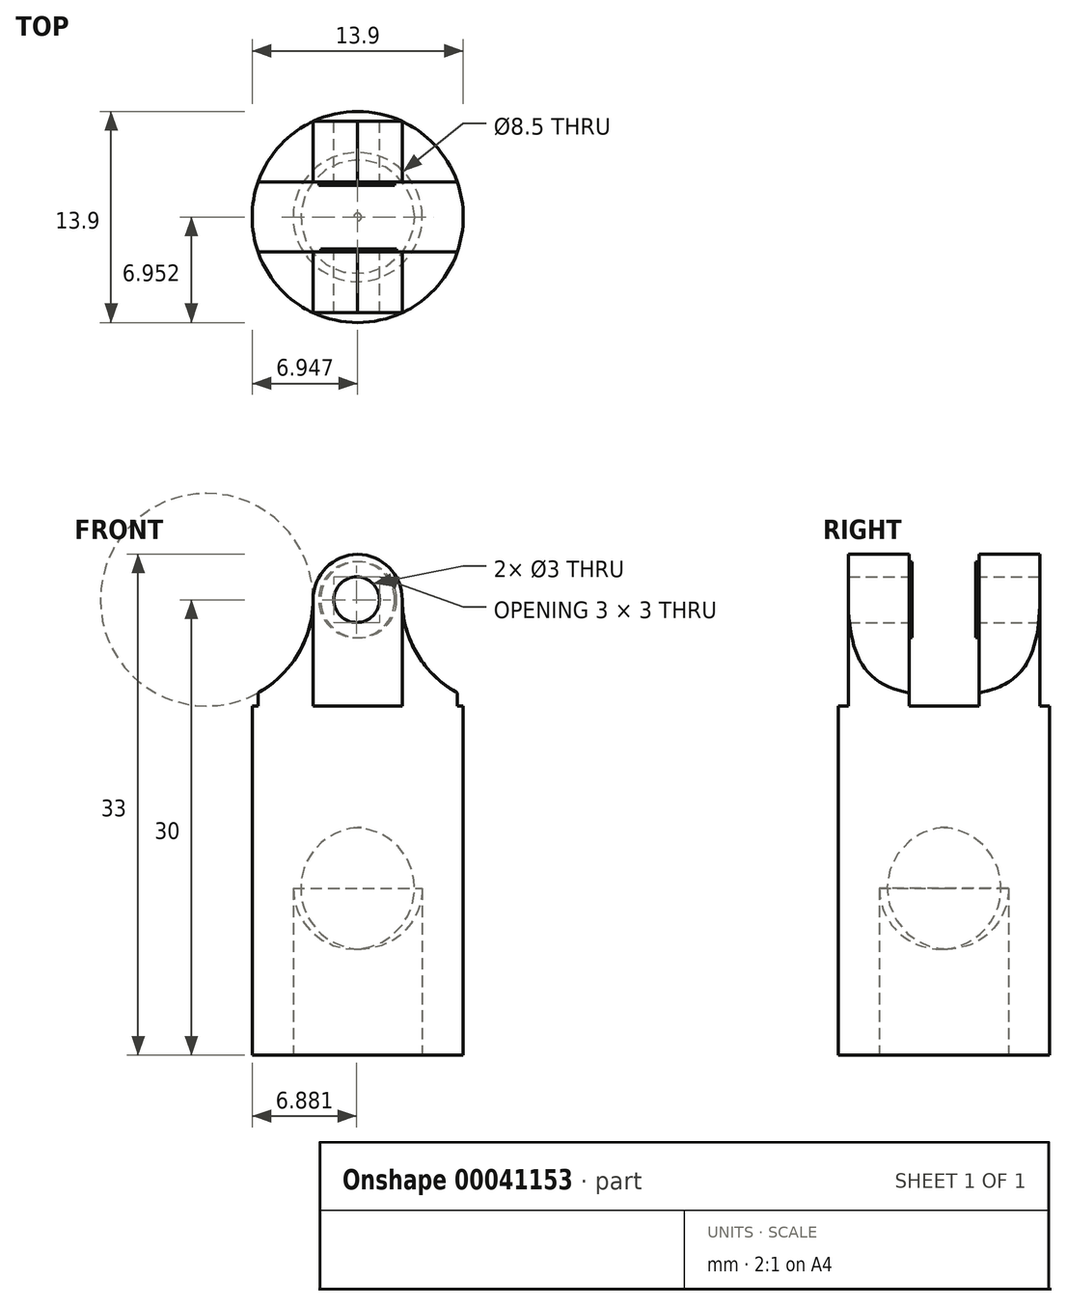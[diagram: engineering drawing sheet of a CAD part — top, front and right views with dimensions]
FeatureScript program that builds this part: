
annotation { "Feature Type Name" : "Feature", "Feature Type Description" : "" }
export const myFeature = defineFeature(function(context is Context, id is Id, definition is map)
    precondition{}
    {
        {
            var Q0;
            Q0=qCreatedBy(makeId("Top.planeOp"),FACE);
            var sketch = newSketch(context, id + "F0", { "sketchPlane" : qUnion([Q0])});
            skLineSegment(sketch, "E0", {"start": v(0, -0.07) * mm, "end": v(-0.27, -0.07) * mm});
            skPoint(sketch, "E1.visualSharp", {"position": v(-9.62, 20.9) * mm});
            skCircle(sketch, "E2", {"center": v(-16.02, 6.95) * mm, "radius": 6.95 * mm});
            skSolve(sketch);
        }
        {
            var Q0;
            Q0 = qSketchRegion(id + "F0", true);
            extrude(context, id + "F1", {"entities" : qUnion([Q0]), "depth" : 23 * mm});
        }
        {
            var Q0;
            Q0=makeQuery(id+"F1.opExtrude","CAP_FACE",FACE,{"disambiguationData":[OSD([sQuery(id+"F0.wireOp",EDGE,"E2")])],"isStart":false});
            var sketch = newSketch(context, id + "F2", { "sketchPlane" : qUnion([Q0])});
            skLineSegment(sketch, "E3", {"start": v(-16.02, 6.95) * mm, "end": v(-9.07, 6.95) * mm});
            skLineSegment(sketch, "E4", {"start": v(-16.02, 6.95) * mm, "end": v(-22.97, 6.95) * mm});
            skLineSegment(sketch, "E5", {"start": v(-22.58, 4.65) * mm, "end": v(-9.47, 4.65) * mm});
            skLineSegment(sketch, "E6", {"start": v(-9.47, 9.25) * mm, "end": v(-22.58, 9.25) * mm});
            skLineSegment(sketch, "E7", {"start": v(-16.02, 6.95) * mm, "end": v(-16.02, 0) * mm});
            skLineSegment(sketch, "E8", {"start": v(-13.09, 0.65) * mm, "end": v(-18.96, 0.65) * mm});
            skLineSegment(sketch, "E9", {"start": v(-13.09, 13.25) * mm, "end": v(-18.96, 13.25) * mm});
            skLineSegment(sketch, "E10", {"start": v(-16.02, 6.95) * mm, "end": v(-16.02, 13.25) * mm});
            skLineSegment(sketch, "E11", {"start": v(-13.09, 13.25) * mm, "end": v(-13.09, 9.25) * mm});
            skLineSegment(sketch, "E12", {"start": v(-13.09, 0.65) * mm, "end": v(-13.09, 4.65) * mm});
            skLineSegment(sketch, "E13", {"start": v(-18.96, 0.65) * mm, "end": v(-18.96, 4.65) * mm});
            skLineSegment(sketch, "E14", {"start": v(-18.96, 13.25) * mm, "end": v(-18.96, 9.25) * mm});
            skSolve(sketch);
        }
        {
            var Q0;
            Q0 = qSketchRegion(id + "F2", true);
            extrude(context, id + "F3", {"entities" : qUnion([Q0]), "operationType" : NewBodyOperationType.ADD, "depth" : 10 * mm});
        }
        {
            var Q0;
            Q0=makeQuery(id+"F3.opExtrude","CAP_EDGE",EDGE,{"disambiguationData":[OSD([sQuery(id+"F2.wireOp",EDGE,"E12")])],"isStart":false});
            var Q1;
            Q1=makeQuery(id+"F3.opExtrude","CAP_EDGE",EDGE,{"disambiguationData":[OSD([sQuery(id+"F2.wireOp",EDGE,"E11")])],"isStart":false});
            var Q2;
            Q2=makeQuery(id+"F3.opExtrude","CAP_EDGE",EDGE,{"disambiguationData":[OSD([sQuery(id+"F2.wireOp",EDGE,"E14")])],"isStart":false});
            var Q3;
            Q3=makeQuery(id+"F3.opExtrude","CAP_EDGE",EDGE,{"disambiguationData":[OSD([sQuery(id+"F2.wireOp",EDGE,"E13")])],"isStart":false});
            fillet(context, id + "F4", {"entities" : qUnion([Q0, Q1, Q2, Q3]), "radius" : 3 * mm, "tangentPropagation" : true, "allowEdgeOverflow" : false});
        }
        {
            var Q0;
            Q0=makeQuery(id+"F3.opExtrude","CAP_EDGE",EDGE,{"disambiguationData":[OSD([sQuery(id+"F2.wireOp",EDGE,"E12")])],"isStart":true});
            var Q1;
            Q1=makeQuery(id+"F3.opExtrude","CAP_EDGE",EDGE,{"disambiguationData":[OSD([sQuery(id+"F2.wireOp",EDGE,"E11")])],"isStart":true});
            var Q2;
            Q2=makeQuery(id+"F3.opExtrude","CAP_EDGE",EDGE,{"disambiguationData":[OSD([sQuery(id+"F2.wireOp",EDGE,"E14")])],"isStart":true});
            var Q3;
            Q3=makeQuery(id+"F3.opExtrude","CAP_EDGE",EDGE,{"disambiguationData":[OSD([sQuery(id+"F2.wireOp",EDGE,"E13")])],"isStart":true});
            fillet(context, id + "F5", {"entities" : qUnion([Q0, Q1, Q2, Q3]), "radius" : 7 * mm, "tangentPropagation" : true, "allowEdgeOverflow" : false});
        }
        {
            var Q0;
            Q0=makeQuery(id+"F1.opExtrude","CAP_FACE",FACE,{"disambiguationData":[OSD([sQuery(id+"F0.wireOp",EDGE,"E2")])],"isStart":true});
            var sketch = newSketch(context, id + "F6", { "sketchPlane" : qUnion([Q0])});
            skCircle(sketch, "E15", {"center": v(-16.02, -6.95) * mm, "radius": 4.25 * mm});
            skSolve(sketch);
        }
        {
            var Q0;
            Q0 = qSketchRegion(id + "F6", true);
            extrude(context, id + "F7", {"entities" : qUnion([Q0]), "operationType" : NewBodyOperationType.REMOVE, "oppositeDirection" : true, "depth" : 15 * mm});
        }
        {
            var Q0;
            Q0=makeQuery(id+"F7.boolean.opBoolean","COPY",EDGE,{"derivedFrom":makeQuery(id+"F7.opExtrude","CAP_EDGE",EDGE,{"disambiguationData":[OSD([sQuery(id+"F6.wireOp",EDGE,"E15")])],"isStart":false})});
            fillet(context, id + "F8", {"entities" : qUnion([Q0]), "radius" : 4 * mm, "tangentPropagation" : true, "allowEdgeOverflow" : false});
        }
        {
            var Q0;
            Q0=makeQuery(id+"F3.opExtrude","SWEPT_FACE",FACE,{"disambiguationData":[OSD([sQuery(id+"F2.wireOp",EDGE,"E9")])]});
            var sketch = newSketch(context, id + "F9", { "sketchPlane" : qUnion([Q0])});
            skCircle(sketch, "E16", {"center": v(16.09, 30) * mm, "radius": 1.5 * mm});
            skSolve(sketch);
        }
        {
            var Q0;
            Q0=makeQuery(id+"F3.opExtrude","SWEPT_FACE",FACE,{"disambiguationData":[OSD([sQuery(id+"F2.wireOp",EDGE,"E5")])]});
            var sketch = newSketch(context, id + "F10", { "sketchPlane" : qUnion([Q0])});
            skCircle(sketch, "E17", {"center": v(15.96, 30) * mm, "radius": 2.5 * mm});
            skSolve(sketch);
        }
        {
            var Q0;
            Q0 = qSketchRegion(id + "F10", true);
            extrude(context, id + "F11", {"entities" : qUnion([Q0]), "operationType" : NewBodyOperationType.ADD, "depth" : 0.2 * mm});
        }
        {
            var Q0;
            Q0=makeQuery(id+"F3.opExtrude","SWEPT_FACE",FACE,{"disambiguationData":[OSD([sQuery(id+"F2.wireOp",EDGE,"E6")])]});
            var sketch = newSketch(context, id + "F12", { "sketchPlane" : qUnion([Q0])});
            skCircle(sketch, "E18", {"center": v(-16.09, 30) * mm, "radius": 2.5 * mm});
            skSolve(sketch);
        }
        {
            var Q0;
            Q0 = qSketchRegion(id + "F12", true);
            extrude(context, id + "F13", {"entities" : qUnion([Q0]), "operationType" : NewBodyOperationType.ADD, "depth" : 0.2 * mm});
        }
        {
            var Q0;
            Q0 = qSketchRegion(id + "F9", true);
            extrude(context, id + "F14", {"entities" : qUnion([Q0]), "operationType" : NewBodyOperationType.REMOVE, "endBound" : BoundingType.THROUGH_ALL, "oppositeDirection" : true, "depth" : 25 * mm});
        }
    });
